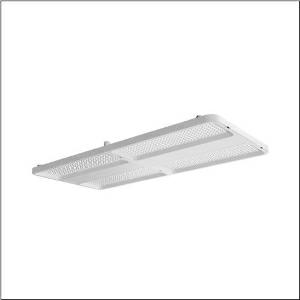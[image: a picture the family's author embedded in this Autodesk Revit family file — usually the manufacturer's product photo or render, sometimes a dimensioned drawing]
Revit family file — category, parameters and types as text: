
# Revit family: highbay_11_maxi_51hn12db4qda
name_source: partatom
category: Lighting Fixtures
units: mm (PartAtom-declared; Revit-internal decimal feet)

## family parameters
Cut with Voids When Loaded = No
Host = Face
Light Source = No
Part Type = Normal
Room Calculation Point = No
Round Connector Dimension = Use Diameter
Shared = No

## types (1)
- --- (1 x LED, 5620 lm, 27.8 W, 4000K)
    Apparent Load = 28 VA
    CIE Flux Codes = 87 98 100 100 100
    Color Rendering = 80
    Color Temperature = 4000K
    Default Elevation = 1800 mm
    Description = high bay luminaire Highbay 11 maxi; direct symmetric wide distribution, light control with lens of PMMA; UGR ≤ 22 (X = 4H | Y = 8H | S = 0.25H | reflection values 70/50/20); luminous flux: 36.000lm; light colour: 840, colour temperature: 4000K, MacAdam ≤ 2 SDCM (initial), colour rendering: CRI > 80; luminous efficacy: 202,6lm/W; rated service life: 100.000h (L95/B50) at AT= 25°C; control: DALI 2; housing frame of high-performance plastic PA6, matt traffic white (RAL 9016); cover of PMMA; dimension (LxWxH): 946 x 442 x 72mm; luminaire connection: terminal, 5-pole, max. 2.5mm² (cable entry for one cable, Ø 8.5..16mm); mains connection: 230..240V, AC/DC 0/50..60Hz; connected load: 177,7W; protection rating (complete): IP66; insulation class (complete): insulation class I (protective earthing); protection symbol: D; impact resistance: IK08; halogen-free wiring; for central battery installations according to DIN EN 60598-2-22; corresponds to IFS (International Featured Standards) requirements for safety and quality in the food industry; LABS conformity tested according to VDMA 24364:2018-05; certification: CE, ENEC, VDE, UKCA; permissible operating ambient temperature: -40..+55°C (reducing of maximum allowable ambient temperature of 5°C with ceiling mounting); packaging unit: 1 piece; (delivery without accessories; please order mounting accessories separately)
    Height = 72 mm  [stored 0.23622 ft]
    Lamp = 1 x LED
    Lamp Light Flux = 5620 lm
    Lamp Power = 27.8 W
    Lamp count = 1
    Length = 946 mm
    Luminous efficacy = 202 lm/W
    Manufacturer = Siteco
    ModVariant = No
    Model = 51HN12DB4QDA
    Mounting Place = Ceiling
    Mounting Type = Pendant
    Number of Poles = 1
    OnlyDefault = Yes
    Power Factor = 1
    Product Name = Highbay 11 maxi
    Product group = high bay luminaire
    ProductGroupID = 901
    Protection Class = Protection class I
    Protection Degree = IP 66
    RLX_Detail_Level = 1
    RLX_Emergency_Light_Flux = 0 lm
    RLX_Emergency_Type = 0
    RLX_Emergency_Type_DB = No
    RlxData = <blob elided: 22261 chars, md5=1f3ece09>
    Socket = socket
    Standby Power = 0 W
    System Light Flux = 5620 lm
    System Power = 28 W
    Type Comments = : DC mode (central or group accumulator) initial emergency light level
    Type Image = l_1363244.jpg
    URL = http://relux.com
    VarID = @adj_005163
    Voltage = 0 V
    Weight = 0.00 kg
    Width = 442 mm

note: [stored X ft] marks values corroborated as IEEE doubles in the binary element streams (Revit-internal decimal feet)

## geometry (parser evidence)
native form markers: Blend x4, Sweep x10
no freeform markers — native parametric forms only
